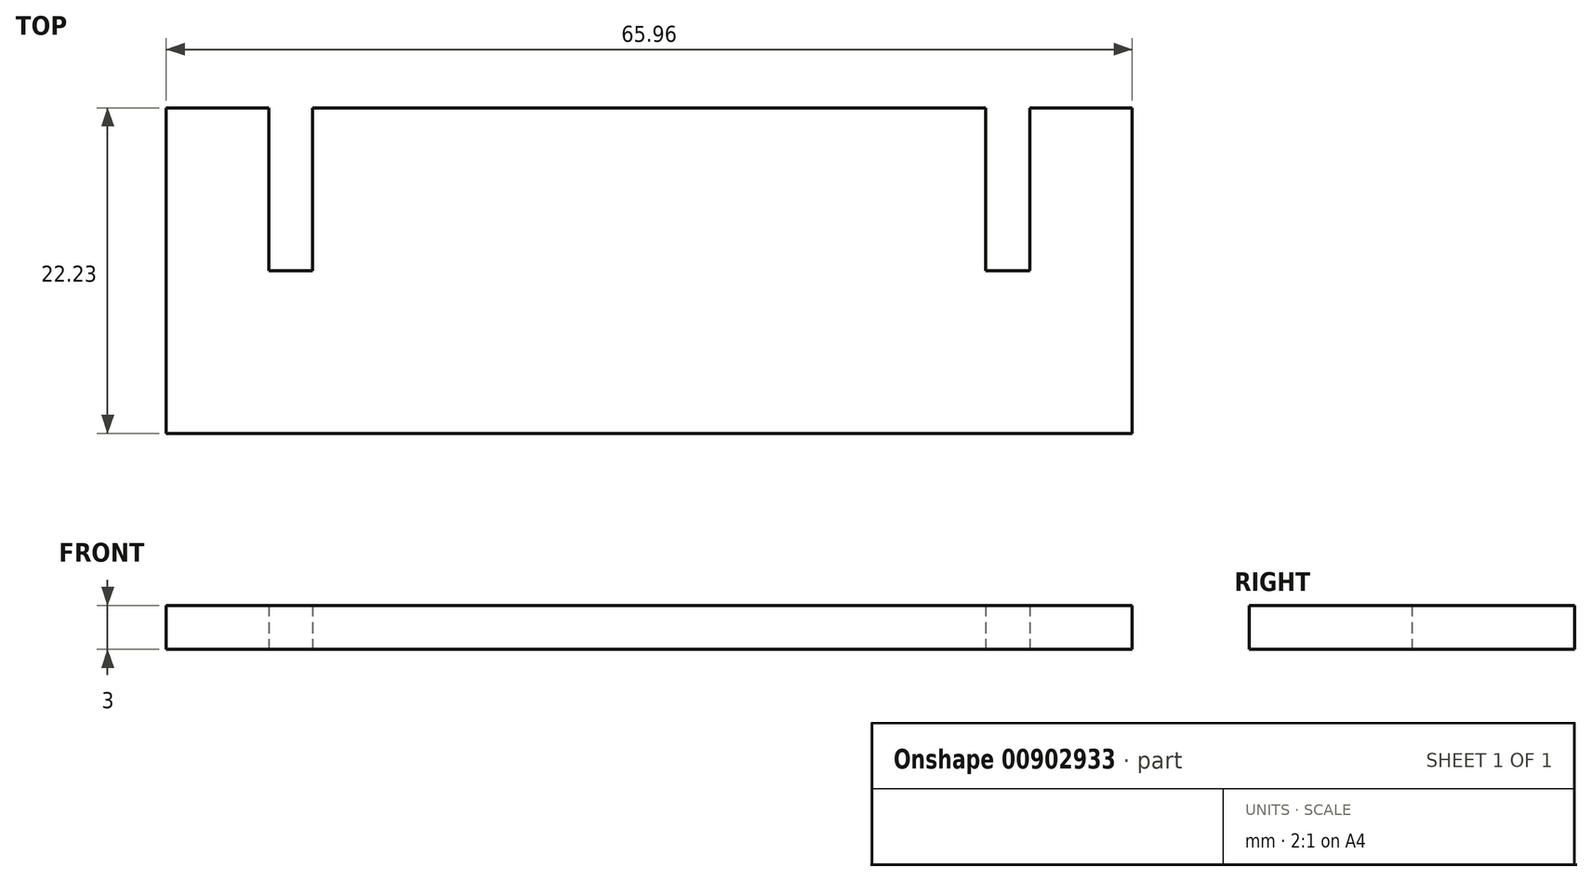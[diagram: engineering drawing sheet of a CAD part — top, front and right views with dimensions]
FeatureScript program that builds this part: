
annotation { "Feature Type Name" : "Feature", "Feature Type Description" : "" }
export const myFeature = defineFeature(function(context is Context, id is Id, definition is map)
    precondition{}
    {
        {
            var Q0;
            Q0=qCreatedBy(makeId("Top.planeOp"),FACE);
            var sketch = newSketch(context, id + "F0", { "sketchPlane" : qUnion([Q0])});
            skLineSegment(sketch, "E0.bottom", {"start": v(38.08, -26.66) * mm, "end": v(-46.42, -26.66) * mm});
            skLineSegment(sketch, "E0.top", {"start": v(38.08, 27.64) * mm, "end": v(-46.42, 27.64) * mm});
            skLineSegment(sketch, "E0.left", {"start": v(38.08, -26.66) * mm, "end": v(38.08, 27.64) * mm});
            skLineSegment(sketch, "E0.right", {"start": v(-46.42, -26.66) * mm, "end": v(-46.42, 27.64) * mm});
            skLineSegment(sketch, "E1.bottom", {"start": v(-46.42, 27.64) * mm, "end": v(-37.42, 27.64) * mm});
            skLineSegment(sketch, "E2.bottom", {"start": v(-37.42, 18.1) * mm, "end": v(-28.42, 18.1) * mm});
            skLineSegment(sketch, "E2.top", {"start": v(-37.42, 27.64) * mm, "end": v(-28.42, 27.64) * mm});
            skLineSegment(sketch, "E2.right", {"start": v(-28.42, 18.1) * mm, "end": v(-28.42, 27.64) * mm});
            skLineSegment(sketch, "E3.left", {"start": v(-37.42, 18.1) * mm, "end": v(-37.42, -17.12) * mm});
            skLineSegment(sketch, "E3.right", {"start": v(-46.42, 18.1) * mm, "end": v(-46.42, -17.12) * mm});
            skLineSegment(sketch, "E4.bottom", {"start": v(-37.42, -17.12) * mm, "end": v(28.54, -17.12) * mm});
            skLineSegment(sketch, "E4.top", {"start": v(-46.42, -26.66) * mm, "end": v(38.08, -26.66) * mm});
            skLineSegment(sketch, "E4.left", {"start": v(-46.42, -17.12) * mm, "end": v(-46.42, -26.66) * mm});
            skLineSegment(sketch, "E4.right", {"start": v(38.08, -17.12) * mm, "end": v(38.08, -26.66) * mm});
            skLineSegment(sketch, "E5", {"start": v(-28.42, 18.1) * mm, "end": v(28.54, 18.1) * mm});
            skLineSegment(sketch, "E6.bottom", {"start": v(38.08, -26.66) * mm, "end": v(28.54, -26.66) * mm});
            skLineSegment(sketch, "E6.top", {"start": v(38.08, 27.64) * mm, "end": v(28.54, 27.64) * mm});
            skLineSegment(sketch, "E6.right", {"start": v(28.54, -17.12) * mm, "end": v(28.54, 18.1) * mm});
            skLineSegment(sketch, "E7", {"start": v(-37.42, 5.1) * mm, "end": v(28.54, 5.1) * mm});
            skLineSegment(sketch, "E8.bottom", {"start": v(-46.42, 24.38) * mm, "end": v(-39.92, 24.38) * mm});
            skLineSegment(sketch, "E8.top", {"start": v(-46.42, 21.38) * mm, "end": v(-39.92, 21.38) * mm});
            skLineSegment(sketch, "E8.left", {"start": v(-46.42, 24.38) * mm, "end": v(-46.42, 21.38) * mm});
            skLineSegment(sketch, "E8.right", {"start": v(-39.92, 24.38) * mm, "end": v(-39.92, 21.38) * mm});
            skLineSegment(sketch, "E9.bottom", {"start": v(-46.42, -23.39) * mm, "end": v(-35.3, -23.39) * mm});
            skLineSegment(sketch, "E9.top", {"start": v(-46.42, -20.39) * mm, "end": v(-35.3, -20.39) * mm});
            skLineSegment(sketch, "E9.left", {"start": v(-46.42, -23.39) * mm, "end": v(-46.42, -20.39) * mm});
            skLineSegment(sketch, "E9.right", {"start": v(-35.3, -23.39) * mm, "end": v(-35.3, -20.39) * mm});
            skLineSegment(sketch, "E10.bottom", {"start": v(-30.42, 5.1) * mm, "end": v(-27.42, 5.1) * mm});
            skLineSegment(sketch, "E10.top", {"start": v(-30.42, 11.6) * mm, "end": v(-27.42, 11.6) * mm});
            skLineSegment(sketch, "E10.left", {"start": v(-30.42, 5.1) * mm, "end": v(-30.42, 11.6) * mm});
            skLineSegment(sketch, "E10.right", {"start": v(-27.42, 5.1) * mm, "end": v(-27.42, 11.6) * mm});
            skLineSegment(sketch, "E11.bottom", {"start": v(21.54, 5.1) * mm, "end": v(18.54, 5.1) * mm});
            skLineSegment(sketch, "E11.top", {"start": v(21.54, 11.6) * mm, "end": v(18.54, 11.6) * mm});
            skLineSegment(sketch, "E11.left", {"start": v(21.54, 5.1) * mm, "end": v(21.54, 11.6) * mm});
            skLineSegment(sketch, "E11.right", {"start": v(18.54, 5.1) * mm, "end": v(18.54, 11.6) * mm});
            skLineSegment(sketch, "E12.bottom", {"start": v(-27.42, 5.1) * mm, "end": v(-30.42, 5.1) * mm});
            skLineSegment(sketch, "E12.top", {"start": v(-27.42, -6) * mm, "end": v(-30.42, -6) * mm});
            skLineSegment(sketch, "E12.left", {"start": v(-27.42, 5.1) * mm, "end": v(-27.42, -6) * mm});
            skLineSegment(sketch, "E12.right", {"start": v(-30.42, 5.1) * mm, "end": v(-30.42, -6) * mm});
            skLineSegment(sketch, "E13.bottom", {"start": v(18.54, 5.1) * mm, "end": v(21.54, 5.1) * mm});
            skLineSegment(sketch, "E13.top", {"start": v(18.54, -6) * mm, "end": v(21.54, -6) * mm});
            skLineSegment(sketch, "E13.left", {"start": v(18.54, 5.1) * mm, "end": v(18.54, -6) * mm});
            skLineSegment(sketch, "E13.right", {"start": v(21.54, 5.1) * mm, "end": v(21.54, -6) * mm});
            skLineSegment(sketch, "E14.bottom", {"start": v(28.54, -17.12) * mm, "end": v(19.54, -17.12) * mm});
            skLineSegment(sketch, "E14.top", {"start": v(28.54, -26.66) * mm, "end": v(19.54, -26.66) * mm});
            skLineSegment(sketch, "E14.right", {"start": v(19.54, -17.12) * mm, "end": v(19.54, -26.66) * mm});
            skLineSegment(sketch, "E15.bottom", {"start": v(38.08, 24.38) * mm, "end": v(26.96, 24.38) * mm});
            skLineSegment(sketch, "E15.top", {"start": v(38.08, 21.38) * mm, "end": v(26.96, 21.38) * mm});
            skLineSegment(sketch, "E15.left", {"start": v(38.08, 24.38) * mm, "end": v(38.08, 21.38) * mm});
            skLineSegment(sketch, "E15.right", {"start": v(26.96, 24.38) * mm, "end": v(26.96, 21.38) * mm});
            skLineSegment(sketch, "E16.bottom", {"start": v(38.08, -20.39) * mm, "end": v(31.58, -20.39) * mm});
            skLineSegment(sketch, "E16.top", {"start": v(38.08, -23.39) * mm, "end": v(31.58, -23.39) * mm});
            skLineSegment(sketch, "E16.left", {"start": v(38.08, -20.39) * mm, "end": v(38.08, -23.39) * mm});
            skLineSegment(sketch, "E16.right", {"start": v(31.58, -20.39) * mm, "end": v(31.58, -23.39) * mm});
            skSolve(sketch);
        }
        {
            var Q0;
            {var subQ9=sQuery(id+"F0.wireOp",EDGE,"E4.bottom");Q0=makeQuery(id+"F0.imprint","IMPRINT",FACE,{"disambiguationData":[TD([[makeQuery(id+"F0.imprint","IMPRINT",EDGE,{"derivedFrom":subQ9}),1.0]])]});}
            extrude(context, id + "F1", {"entities" : qUnion([Q0]), "depth" : 3 * mm, "offsetDistance" : 25 * mm});
        }
    });
